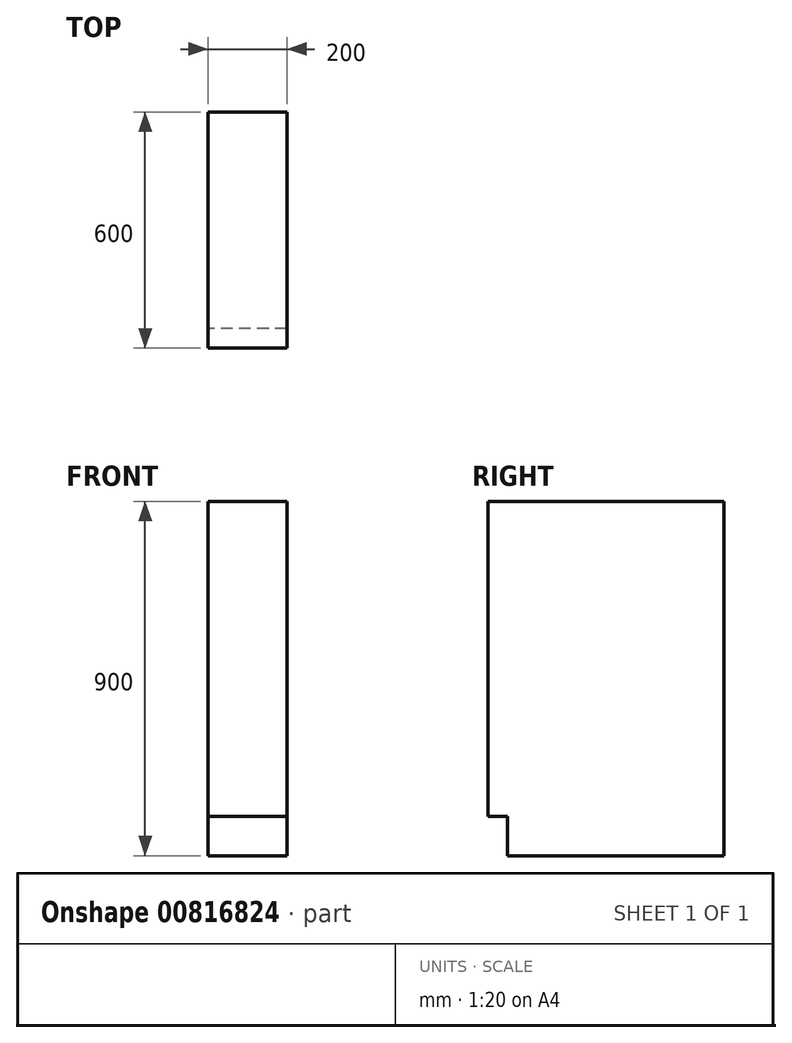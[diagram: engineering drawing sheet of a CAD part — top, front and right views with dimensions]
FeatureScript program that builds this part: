
annotation { "Feature Type Name" : "Feature", "Feature Type Description" : "" }
export const myFeature = defineFeature(function(context is Context, id is Id, definition is map)
    precondition{}
    {
        {
            var Q0;
            Q0=qCreatedBy(makeId("Front.planeOp"),FACE);
            var sketch = newSketch(context, id + "F0", { "sketchPlane" : qUnion([Q0])});
            skLineSegment(sketch, "E0.bottom", {"start": v(0, 0) * mm, "end": v(-200, 0) * mm});
            skLineSegment(sketch, "E0.top", {"start": v(0, 800) * mm, "end": v(-200, 800) * mm});
            skLineSegment(sketch, "E0.left", {"start": v(0, 0) * mm, "end": v(0, 800) * mm});
            skLineSegment(sketch, "E0.right", {"start": v(-200, 0) * mm, "end": v(-200, 800) * mm});
            skSolve(sketch);
        }
        {
            var Q0;
            Q0=makeQuery(id+"F0.imprint","IMPRINT",FACE,{"disambiguationData":[TD([[makeQuery(id+"F0.imprint","IMPRINT",EDGE,{"derivedFrom":sQuery(id+"F0.wireOp",EDGE,"E0.bottom")}),-1.0]])]});
            extrude(context, id + "F1", {"entities" : qUnion([Q0]), "depth" : 600 * mm, "offsetDistance" : 25 * mm});
        }
        {
            var Q0;
            Q0=qCreatedBy(makeId("Front.planeOp"),FACE);
            var sketch = newSketch(context, id + "F2", { "sketchPlane" : qUnion([Q0])});
            skLineSegment(sketch, "E1.bottom", {"start": v(0, 0) * mm, "end": v(-200, 0) * mm});
            skLineSegment(sketch, "E1.top", {"start": v(0, -100) * mm, "end": v(-200, -100) * mm});
            skLineSegment(sketch, "E1.left", {"start": v(0, 0) * mm, "end": v(0, -100) * mm});
            skLineSegment(sketch, "E1.right", {"start": v(-200, 0) * mm, "end": v(-200, -100) * mm});
            skSolve(sketch);
        }
        {
            var Q0;
            Q0=qSketchRegion(id+"F2",true);
            extrude(context, id + "F3", {"entities" : qUnion([Q0]), "operationType" : NewBodyOperationType.ADD, "depth" : 550 * mm, "offsetDistance" : 25 * mm});
        }
    });
